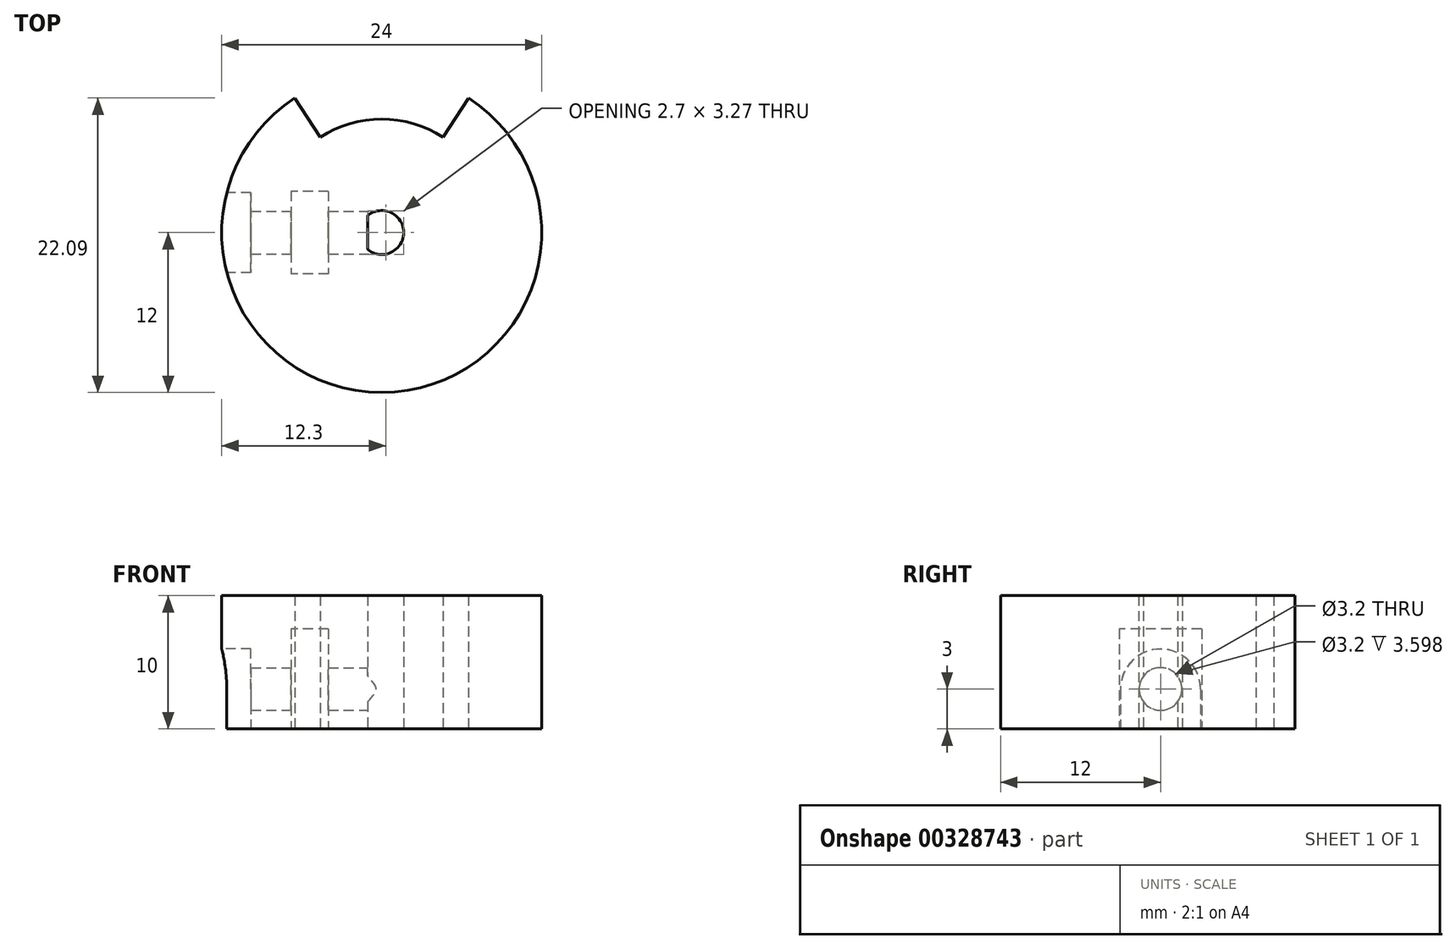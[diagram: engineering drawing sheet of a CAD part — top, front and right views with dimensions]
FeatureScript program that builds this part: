
annotation { "Feature Type Name" : "Feature", "Feature Type Description" : "" }
export const myFeature = defineFeature(function(context is Context, id is Id, definition is map)
    precondition{}
    {
        {
            var Q0;
            Q0=qCreatedBy(makeId("Top.planeOp"),FACE);
            var sketch = newSketch(context, id + "F0", { "sketchPlane" : qUnion([Q0])});
            skArc(sketch, "E0", {"start": v(-6.5, 10.09) * mm, "mid": v(0, -12) * mm, "end": v(6.5, 10.09) * mm});
            skArc(sketch, "E1", {"start": v(4.6, 7.15) * mm, "mid": v(0, 8.5) * mm, "end": v(-4.6, 7.15) * mm});
            skLineSegment(sketch, "E2", {"start": v(4.6, 7.15) * mm, "end": v(6.5, 10.09) * mm});
            skLineSegment(sketch, "E3", {"start": v(-4.6, 7.15) * mm, "end": v(-6.5, 10.09) * mm});
            skLineSegment(sketch, "E4", {"start": v(-6.5, 10.09) * mm, "end": v(6.5, 10.09) * mm, "construction": true});
            skArc(sketch, "E5", {"start": v(-1.05, -1.27) * mm, "mid": v(1.65, 0) * mm, "end": v(-1.05, 1.27) * mm});
            skLineSegment(sketch, "E6", {"start": v(-1.05, 1.27) * mm, "end": v(-1.05, -1.27) * mm});
            skSolve(sketch);
        }
        {
            var Q0;
            Q0=makeQuery(id+"F0.imprint","IMPRINT",FACE,{"disambiguationData":[TD([[makeQuery(id+"F0.imprint","IMPRINT",EDGE,{"derivedFrom":sQuery(id+"F0.wireOp",EDGE,"E0")}),1.0]])]});
            extrude(context, id + "F1", {"entities" : qUnion([Q0]), "depth" : 10 * mm});
        }
        {
            var Q0;
            Q0=qCreatedBy(makeId("Top.planeOp"),FACE);
            var sketch = newSketch(context, id + "F2", { "sketchPlane" : qUnion([Q0])});
            skLineSegment(sketch, "E7.bottom", {"start": v(-4, 3.1) * mm, "end": v(-6.8, 3.1) * mm});
            skLineSegment(sketch, "E7.top", {"start": v(-4, -3.1) * mm, "end": v(-6.8, -3.1) * mm});
            skLineSegment(sketch, "E7.left", {"start": v(-4, 3.1) * mm, "end": v(-4, -3.1) * mm});
            skLineSegment(sketch, "E7.right", {"start": v(-6.8, 3.1) * mm, "end": v(-6.8, -3.1) * mm});
            skLineSegment(sketch, "E8", {"start": v(0, 0) * mm, "end": v(-4, 0) * mm});
            skSolve(sketch);
        }
        {
            var Q0;
            Q0 = qSketchRegion(id + "F2", true);
            extrude(context, id + "F3", {"entities" : qUnion([Q0]), "operationType" : NewBodyOperationType.REMOVE, "depth" : 7.5 * mm});
        }
        {
            var Q0;
            Q0=qCreatedBy(makeId("Right.planeOp"),FACE);
            var sketch = newSketch(context, id + "F4", { "sketchPlane" : qUnion([Q0])});
            skLineSegment(sketch, "E9", {"start": v(0, 0) * mm, "end": v(0, 3) * mm});
            skCircle(sketch, "E10", {"center": v(0, 3) * mm, "radius": 1.6 * mm});
            skSolve(sketch);
        }
        {
            var Q0;
            Q0 = qSketchRegion(id + "F4", true);
            extrude(context, id + "F5", {"entities" : qUnion([Q0]), "operationType" : NewBodyOperationType.REMOVE, "oppositeDirection" : true, "depth" : 25 * mm});
        }
        {
            var Q0;
            Q0=makeQuery(id+"F3.boolean.opBoolean","COPY",FACE,{"derivedFrom":makeQuery(id+"F3.opExtrude","SWEPT_FACE",FACE,{"disambiguationData":[OSD([sQuery(id+"F2.wireOp",EDGE,"E7.left")])]})});
            cPlane(context, id + "F6", {"entities" : qUnion([Q0]), "cplaneType" : CPlaneType.OFFSET, "offset" : 8 * mm, "width" : 150 * mm, "height" : 150 * mm});
        }
        {
            var Q0;
            Q0=qCreatedBy(id+"F6.planeOp",FACE);
            var sketch = newSketch(context, id + "F7", { "sketchPlane" : qUnion([Q0])});
            skArc(sketch, "E11", {"start": v(3, 3) * mm, "mid": v(0, 6) * mm, "end": v(-3, 3) * mm});
            skLineSegment(sketch, "E12.top", {"start": v(3, -2.97) * mm, "end": v(-3, -2.97) * mm});
            skLineSegment(sketch, "E12.left", {"start": v(3, 3) * mm, "end": v(3, -2.97) * mm});
            skLineSegment(sketch, "E12.right", {"start": v(-3, 3) * mm, "end": v(-3, -2.97) * mm});
            skSolve(sketch);
        }
        {
            var Q0;
            Q0 = qSketchRegion(id + "F7", true);
            extrude(context, id + "F8", {"entities" : qUnion([Q0]), "operationType" : NewBodyOperationType.REMOVE, "oppositeDirection" : true, "depth" : 2.2 * mm});
        }
    });
